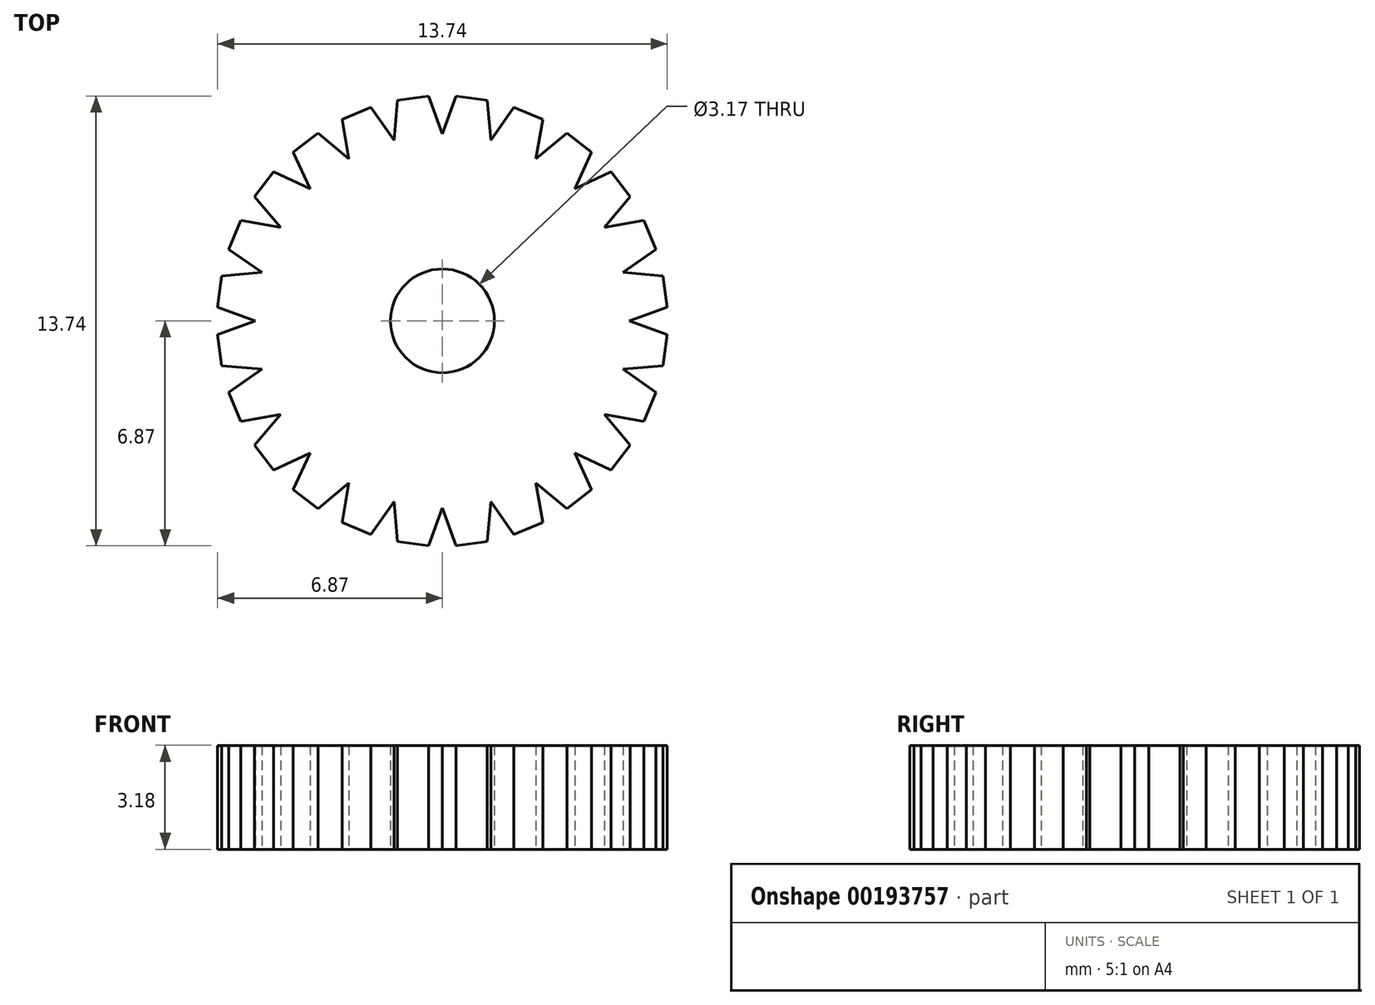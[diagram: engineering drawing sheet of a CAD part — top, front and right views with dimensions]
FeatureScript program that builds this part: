
annotation { "Feature Type Name" : "Feature", "Feature Type Description" : "" }
export const myFeature = defineFeature(function(context is Context, id is Id, definition is map)
    precondition{}
    {
        {
            var Q0;
            Q0=qCreatedBy(makeId("Top.planeOp"),FACE);
            var sketch = newSketch(context, id + "F0", { "sketchPlane" : qUnion([Q0])});
            skCircle(sketch, "E0", {"center": v(0, 0) * mm, "radius": 6.35 * mm});
            skCircle(sketch, "E1", {"center": v(0, 0) * mm, "radius": 6.88 * mm});
            skCircle(sketch, "E2", {"center": v(0, 0) * mm, "radius": 5.72 * mm});
            skLineSegment(sketch, "E3", {"start": v(0, 0) * mm, "end": v(0, 5.72) * mm});
            skLineSegment(sketch, "E4.1.0", {"start": v(0, 0) * mm, "end": v(-1.48, 5.52) * mm});
            skLineSegment(sketch, "E4.2.0", {"start": v(0, 0) * mm, "end": v(-2.86, 4.95) * mm});
            skLineSegment(sketch, "E4.3.0", {"start": v(0, 0) * mm, "end": v(-4.04, 4.04) * mm});
            skLineSegment(sketch, "E4.4.0", {"start": v(0, 0) * mm, "end": v(-4.95, 2.86) * mm});
            skLineSegment(sketch, "E4.5.0", {"start": v(0, 0) * mm, "end": v(-5.52, 1.48) * mm});
            skLineSegment(sketch, "E4.6.0", {"start": v(0, 0) * mm, "end": v(-5.72, 0) * mm});
            skLineSegment(sketch, "E4.7.0", {"start": v(0, 0) * mm, "end": v(-5.52, -1.48) * mm});
            skLineSegment(sketch, "E4.8.0", {"start": v(0, 0) * mm, "end": v(-4.95, -2.86) * mm});
            skLineSegment(sketch, "E4.9.0", {"start": v(0, 0) * mm, "end": v(-4.04, -4.04) * mm});
            skLineSegment(sketch, "E4.10.0", {"start": v(0, 0) * mm, "end": v(-2.86, -4.95) * mm});
            skLineSegment(sketch, "E4.11.0", {"start": v(0, 0) * mm, "end": v(-1.48, -5.52) * mm});
            skLineSegment(sketch, "E4.12.0", {"start": v(0, 0) * mm, "end": v(0, -5.72) * mm});
            skLineSegment(sketch, "E4.13.0", {"start": v(0, 0) * mm, "end": v(1.48, -5.52) * mm});
            skLineSegment(sketch, "E4.14.0", {"start": v(0, 0) * mm, "end": v(2.86, -4.95) * mm});
            skLineSegment(sketch, "E4.15.0", {"start": v(0, 0) * mm, "end": v(4.04, -4.04) * mm});
            skLineSegment(sketch, "E4.16.0", {"start": v(0, 0) * mm, "end": v(4.95, -2.86) * mm});
            skLineSegment(sketch, "E4.17.0", {"start": v(0, 0) * mm, "end": v(5.52, -1.48) * mm});
            skLineSegment(sketch, "E4.18.0", {"start": v(0, 0) * mm, "end": v(5.72, 0) * mm});
            skLineSegment(sketch, "E4.19.0", {"start": v(0, 0) * mm, "end": v(5.52, 1.48) * mm});
            skLineSegment(sketch, "E4.20.0", {"start": v(0, 0) * mm, "end": v(4.95, 2.86) * mm});
            skLineSegment(sketch, "E4.21.0", {"start": v(0, 0) * mm, "end": v(4.04, 4.04) * mm});
            skLineSegment(sketch, "E4.22.0", {"start": v(0, 0) * mm, "end": v(2.86, 4.95) * mm});
            skLineSegment(sketch, "E4.23.0", {"start": v(0, 0) * mm, "end": v(1.48, 5.52) * mm});
            skSolve(sketch);
        }
        {
            var Q0;
            Q0=qCreatedBy(makeId("Top.planeOp"),FACE);
            var sketch = newSketch(context, id + "F1", { "sketchPlane" : qUnion([Q0])});
            skLineSegment(sketch, "E5", {"start": v(0, 5.72) * mm, "end": v(0.42, 6.87) * mm});
            skLineSegment(sketch, "E6", {"start": v(1.48, 5.52) * mm, "end": v(1.37, 6.75) * mm});
            skLineSegment(sketch, "E7", {"start": v(0.42, 6.87) * mm, "end": v(1.37, 6.75) * mm});
            skLineSegment(sketch, "E8.1.0", {"start": v(-1.48, 5.52) * mm, "end": v(-1.37, 6.75) * mm});
            skLineSegment(sketch, "E8.1.1", {"start": v(-1.37, 6.75) * mm, "end": v(-0.42, 6.87) * mm});
            skLineSegment(sketch, "E8.1.2", {"start": v(0, 5.71) * mm, "end": v(-0.42, 6.87) * mm});
            skLineSegment(sketch, "E8.2.0", {"start": v(-2.86, 4.95) * mm, "end": v(-3.07, 6.16) * mm});
            skLineSegment(sketch, "E8.2.1", {"start": v(-3.07, 6.16) * mm, "end": v(-2.18, 6.53) * mm});
            skLineSegment(sketch, "E8.2.2", {"start": v(-1.48, 5.52) * mm, "end": v(-2.18, 6.53) * mm});
            skLineSegment(sketch, "E8.3.0", {"start": v(-4.04, 4.04) * mm, "end": v(-4.56, 5.16) * mm});
            skLineSegment(sketch, "E8.3.1", {"start": v(-4.56, 5.16) * mm, "end": v(-3.8, 5.74) * mm});
            skLineSegment(sketch, "E8.3.2", {"start": v(-2.86, 4.95) * mm, "end": v(-3.8, 5.74) * mm});
            skLineSegment(sketch, "E8.4.0", {"start": v(-4.95, 2.86) * mm, "end": v(-5.74, 3.8) * mm});
            skLineSegment(sketch, "E8.4.1", {"start": v(-5.74, 3.8) * mm, "end": v(-5.16, 4.56) * mm});
            skLineSegment(sketch, "E8.4.2", {"start": v(-4.04, 4.04) * mm, "end": v(-5.16, 4.56) * mm});
            skLineSegment(sketch, "E8.5.0", {"start": v(-5.52, 1.48) * mm, "end": v(-6.53, 2.18) * mm});
            skLineSegment(sketch, "E8.5.1", {"start": v(-6.53, 2.18) * mm, "end": v(-6.16, 3.07) * mm});
            skLineSegment(sketch, "E8.5.2", {"start": v(-4.95, 2.86) * mm, "end": v(-6.16, 3.07) * mm});
            skLineSegment(sketch, "E8.6.0", {"start": v(-5.72, 0) * mm, "end": v(-6.87, 0.42) * mm});
            skLineSegment(sketch, "E8.6.1", {"start": v(-6.87, 0.42) * mm, "end": v(-6.75, 1.37) * mm});
            skLineSegment(sketch, "E8.6.2", {"start": v(-5.52, 1.48) * mm, "end": v(-6.75, 1.37) * mm});
            skLineSegment(sketch, "E8.7.0", {"start": v(-5.52, -1.48) * mm, "end": v(-6.75, -1.37) * mm});
            skLineSegment(sketch, "E8.7.1", {"start": v(-6.75, -1.37) * mm, "end": v(-6.87, -0.42) * mm});
            skLineSegment(sketch, "E8.7.2", {"start": v(-5.71, 0) * mm, "end": v(-6.87, -0.42) * mm});
            skLineSegment(sketch, "E8.8.0", {"start": v(-4.95, -2.86) * mm, "end": v(-6.16, -3.07) * mm});
            skLineSegment(sketch, "E8.8.1", {"start": v(-6.16, -3.07) * mm, "end": v(-6.53, -2.18) * mm});
            skLineSegment(sketch, "E8.8.2", {"start": v(-5.52, -1.48) * mm, "end": v(-6.53, -2.18) * mm});
            skLineSegment(sketch, "E8.9.0", {"start": v(-4.04, -4.04) * mm, "end": v(-5.16, -4.56) * mm});
            skLineSegment(sketch, "E8.9.1", {"start": v(-5.16, -4.56) * mm, "end": v(-5.74, -3.8) * mm});
            skLineSegment(sketch, "E8.9.2", {"start": v(-4.95, -2.86) * mm, "end": v(-5.74, -3.8) * mm});
            skLineSegment(sketch, "E8.10.0", {"start": v(-2.86, -4.95) * mm, "end": v(-3.8, -5.74) * mm});
            skLineSegment(sketch, "E8.10.1", {"start": v(-3.8, -5.74) * mm, "end": v(-4.56, -5.16) * mm});
            skLineSegment(sketch, "E8.10.2", {"start": v(-4.04, -4.04) * mm, "end": v(-4.56, -5.16) * mm});
            skLineSegment(sketch, "E8.11.0", {"start": v(-1.48, -5.52) * mm, "end": v(-2.18, -6.53) * mm});
            skLineSegment(sketch, "E8.11.1", {"start": v(-2.18, -6.53) * mm, "end": v(-3.07, -6.16) * mm});
            skLineSegment(sketch, "E8.11.2", {"start": v(-2.86, -4.95) * mm, "end": v(-3.07, -6.16) * mm});
            skLineSegment(sketch, "E8.12.0", {"start": v(0, -5.72) * mm, "end": v(-0.42, -6.87) * mm});
            skLineSegment(sketch, "E8.12.1", {"start": v(-0.42, -6.87) * mm, "end": v(-1.37, -6.75) * mm});
            skLineSegment(sketch, "E8.12.2", {"start": v(-1.48, -5.52) * mm, "end": v(-1.37, -6.75) * mm});
            skLineSegment(sketch, "E8.13.0", {"start": v(1.48, -5.52) * mm, "end": v(1.37, -6.75) * mm});
            skLineSegment(sketch, "E8.13.1", {"start": v(1.37, -6.75) * mm, "end": v(0.42, -6.87) * mm});
            skLineSegment(sketch, "E8.13.2", {"start": v(0, -5.71) * mm, "end": v(0.42, -6.87) * mm});
            skLineSegment(sketch, "E8.14.0", {"start": v(2.86, -4.95) * mm, "end": v(3.07, -6.16) * mm});
            skLineSegment(sketch, "E8.14.1", {"start": v(3.07, -6.16) * mm, "end": v(2.18, -6.53) * mm});
            skLineSegment(sketch, "E8.14.2", {"start": v(1.48, -5.52) * mm, "end": v(2.18, -6.53) * mm});
            skLineSegment(sketch, "E8.15.0", {"start": v(4.04, -4.04) * mm, "end": v(4.56, -5.16) * mm});
            skLineSegment(sketch, "E8.15.1", {"start": v(4.56, -5.16) * mm, "end": v(3.8, -5.74) * mm});
            skLineSegment(sketch, "E8.15.2", {"start": v(2.86, -4.95) * mm, "end": v(3.8, -5.74) * mm});
            skLineSegment(sketch, "E8.16.0", {"start": v(4.95, -2.86) * mm, "end": v(5.74, -3.8) * mm});
            skLineSegment(sketch, "E8.16.1", {"start": v(5.74, -3.8) * mm, "end": v(5.16, -4.56) * mm});
            skLineSegment(sketch, "E8.16.2", {"start": v(4.04, -4.04) * mm, "end": v(5.16, -4.56) * mm});
            skLineSegment(sketch, "E8.17.0", {"start": v(5.52, -1.48) * mm, "end": v(6.53, -2.18) * mm});
            skLineSegment(sketch, "E8.17.1", {"start": v(6.53, -2.18) * mm, "end": v(6.16, -3.07) * mm});
            skLineSegment(sketch, "E8.17.2", {"start": v(4.95, -2.86) * mm, "end": v(6.16, -3.07) * mm});
            skLineSegment(sketch, "E8.18.0", {"start": v(5.72, 0) * mm, "end": v(6.87, -0.42) * mm});
            skLineSegment(sketch, "E8.18.1", {"start": v(6.87, -0.42) * mm, "end": v(6.75, -1.37) * mm});
            skLineSegment(sketch, "E8.18.2", {"start": v(5.52, -1.48) * mm, "end": v(6.75, -1.37) * mm});
            skLineSegment(sketch, "E8.19.0", {"start": v(5.52, 1.48) * mm, "end": v(6.75, 1.37) * mm});
            skLineSegment(sketch, "E8.19.1", {"start": v(6.75, 1.37) * mm, "end": v(6.87, 0.42) * mm});
            skLineSegment(sketch, "E8.19.2", {"start": v(5.71, 0) * mm, "end": v(6.87, 0.42) * mm});
            skLineSegment(sketch, "E8.20.0", {"start": v(4.95, 2.86) * mm, "end": v(6.16, 3.07) * mm});
            skLineSegment(sketch, "E8.20.1", {"start": v(6.16, 3.07) * mm, "end": v(6.53, 2.18) * mm});
            skLineSegment(sketch, "E8.20.2", {"start": v(5.52, 1.48) * mm, "end": v(6.53, 2.18) * mm});
            skLineSegment(sketch, "E8.21.0", {"start": v(4.04, 4.04) * mm, "end": v(5.16, 4.56) * mm});
            skLineSegment(sketch, "E8.21.1", {"start": v(5.16, 4.56) * mm, "end": v(5.74, 3.8) * mm});
            skLineSegment(sketch, "E8.21.2", {"start": v(4.95, 2.86) * mm, "end": v(5.74, 3.8) * mm});
            skLineSegment(sketch, "E8.22.0", {"start": v(2.86, 4.95) * mm, "end": v(3.8, 5.74) * mm});
            skLineSegment(sketch, "E8.22.1", {"start": v(3.8, 5.74) * mm, "end": v(4.56, 5.16) * mm});
            skLineSegment(sketch, "E8.22.2", {"start": v(4.04, 4.04) * mm, "end": v(4.56, 5.16) * mm});
            skLineSegment(sketch, "E8.23.0", {"start": v(1.48, 5.52) * mm, "end": v(2.18, 6.53) * mm});
            skLineSegment(sketch, "E8.23.1", {"start": v(2.18, 6.53) * mm, "end": v(3.07, 6.16) * mm});
            skLineSegment(sketch, "E8.23.2", {"start": v(2.86, 4.95) * mm, "end": v(3.07, 6.16) * mm});
            skPoint(sketch, "E8.center", {"position": v(0, 0) * mm});
            skSolve(sketch);
        }
        {
            var Q0;
            Q0 = qSketchRegion(id + "F1", true);
            extrude(context, id + "F2", {"entities" : qUnion([Q0]), "depth" : 3.17 * mm});
        }
        {
            var Q0;
            Q0=sQuery(id+"F0.wireOp",VERTEX,"E0.center");
            var Q1;
            Q1=makeQuery(id+"F2.opExtrude","SWEPT_BODY",BODY,{"disambiguationData":[OSD([sQuery(id+"F1.wireOp",EDGE,"E5"),sQuery(id+"F1.wireOp",EDGE,"E6"),sQuery(id+"F1.wireOp",EDGE,"E7"),sQuery(id+"F1.wireOp",EDGE,"E8.1.0"),sQuery(id+"F1.wireOp",EDGE,"E8.1.1"),sQuery(id+"F1.wireOp",EDGE,"E8.1.2"),sQuery(id+"F1.wireOp",EDGE,"E8.2.0"),sQuery(id+"F1.wireOp",EDGE,"E8.2.1"),sQuery(id+"F1.wireOp",EDGE,"E8.2.2"),sQuery(id+"F1.wireOp",EDGE,"E8.3.0"),sQuery(id+"F1.wireOp",EDGE,"E8.3.1"),sQuery(id+"F1.wireOp",EDGE,"E8.3.2"),sQuery(id+"F1.wireOp",EDGE,"E8.4.0"),sQuery(id+"F1.wireOp",EDGE,"E8.4.1"),sQuery(id+"F1.wireOp",EDGE,"E8.4.2"),sQuery(id+"F1.wireOp",EDGE,"E8.5.0"),sQuery(id+"F1.wireOp",EDGE,"E8.5.1"),sQuery(id+"F1.wireOp",EDGE,"E8.5.2"),sQuery(id+"F1.wireOp",EDGE,"E8.6.0"),sQuery(id+"F1.wireOp",EDGE,"E8.6.1"),sQuery(id+"F1.wireOp",EDGE,"E8.6.2"),sQuery(id+"F1.wireOp",EDGE,"E8.7.0"),sQuery(id+"F1.wireOp",EDGE,"E8.7.1"),sQuery(id+"F1.wireOp",EDGE,"E8.7.2"),sQuery(id+"F1.wireOp",EDGE,"E8.8.0"),sQuery(id+"F1.wireOp",EDGE,"E8.8.1"),sQuery(id+"F1.wireOp",EDGE,"E8.8.2"),sQuery(id+"F1.wireOp",EDGE,"E8.9.0"),sQuery(id+"F1.wireOp",EDGE,"E8.9.1"),sQuery(id+"F1.wireOp",EDGE,"E8.9.2"),sQuery(id+"F1.wireOp",EDGE,"E8.10.0"),sQuery(id+"F1.wireOp",EDGE,"E8.10.1"),sQuery(id+"F1.wireOp",EDGE,"E8.10.2"),sQuery(id+"F1.wireOp",EDGE,"E8.11.0"),sQuery(id+"F1.wireOp",EDGE,"E8.11.1"),sQuery(id+"F1.wireOp",EDGE,"E8.11.2"),sQuery(id+"F1.wireOp",EDGE,"E8.12.0"),sQuery(id+"F1.wireOp",EDGE,"E8.12.1"),sQuery(id+"F1.wireOp",EDGE,"E8.12.2"),sQuery(id+"F1.wireOp",EDGE,"E8.13.0"),sQuery(id+"F1.wireOp",EDGE,"E8.13.1"),sQuery(id+"F1.wireOp",EDGE,"E8.13.2"),sQuery(id+"F1.wireOp",EDGE,"E8.14.0"),sQuery(id+"F1.wireOp",EDGE,"E8.14.1"),sQuery(id+"F1.wireOp",EDGE,"E8.14.2"),sQuery(id+"F1.wireOp",EDGE,"E8.15.0"),sQuery(id+"F1.wireOp",EDGE,"E8.15.1"),sQuery(id+"F1.wireOp",EDGE,"E8.15.2"),sQuery(id+"F1.wireOp",EDGE,"E8.16.0"),sQuery(id+"F1.wireOp",EDGE,"E8.16.1"),sQuery(id+"F1.wireOp",EDGE,"E8.16.2"),sQuery(id+"F1.wireOp",EDGE,"E8.17.0"),sQuery(id+"F1.wireOp",EDGE,"E8.17.1"),sQuery(id+"F1.wireOp",EDGE,"E8.17.2"),sQuery(id+"F1.wireOp",EDGE,"E8.18.0"),sQuery(id+"F1.wireOp",EDGE,"E8.18.1"),sQuery(id+"F1.wireOp",EDGE,"E8.18.2"),sQuery(id+"F1.wireOp",EDGE,"E8.19.0"),sQuery(id+"F1.wireOp",EDGE,"E8.19.1"),sQuery(id+"F1.wireOp",EDGE,"E8.19.2"),sQuery(id+"F1.wireOp",EDGE,"E8.20.0"),sQuery(id+"F1.wireOp",EDGE,"E8.20.1"),sQuery(id+"F1.wireOp",EDGE,"E8.20.2"),sQuery(id+"F1.wireOp",EDGE,"E8.21.0"),sQuery(id+"F1.wireOp",EDGE,"E8.21.1"),sQuery(id+"F1.wireOp",EDGE,"E8.21.2"),sQuery(id+"F1.wireOp",EDGE,"E8.22.0"),sQuery(id+"F1.wireOp",EDGE,"E8.22.1"),sQuery(id+"F1.wireOp",EDGE,"E8.22.2"),sQuery(id+"F1.wireOp",EDGE,"E8.23.0"),sQuery(id+"F1.wireOp",EDGE,"E8.23.1"),sQuery(id+"F1.wireOp",EDGE,"E8.23.2")])]});
            hole(context, id + "F3", {"style" : HoleStyle.SIMPLE, "endStyle" : HoleEndStyle.THROUGH, "oppositeDirection" : true, "holeDiameter" : 3.17 * mm, "locations" : qUnion([Q0]), "scope" : qUnion([Q1]), "isTappedThrough" : true});
        }
    });
